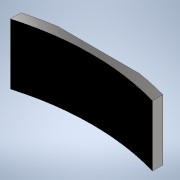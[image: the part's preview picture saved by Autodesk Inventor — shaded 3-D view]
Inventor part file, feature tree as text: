
AUTODESK INVENTOR PART (.ipt)
format: ipt  version: 2022 (Build 260153000, 153)  size: 102,400 bytes
history: native  units: mm
features: extrude x1, sketch x1
ambient origin geometry x8: Origin, YZ Plane, XZ Plane, XY Plane, X Axis, Y Axis, Z Axis, Center Point
bodies: Solid1 (feature_tree)
feature tree (2):
  extrude  "Extrusion1"  Depth=30.0mm
  sketch  "Sketch1"  dims[d0=70.0mm d1=35.0mm d2=5.0mm d3=5.0mm d4=40.0mm d5=30.0mm d6=0.0mm]
